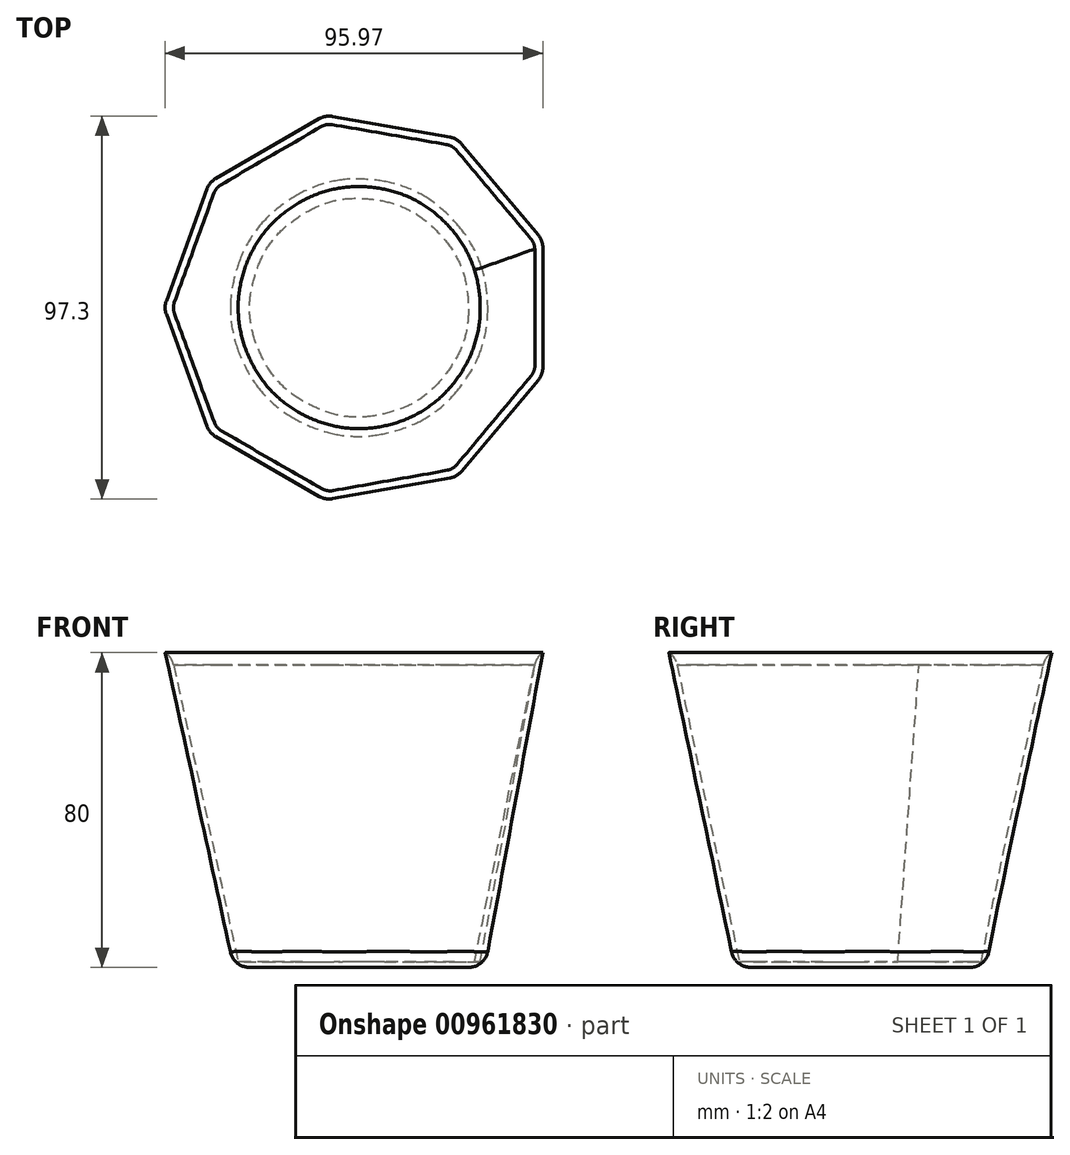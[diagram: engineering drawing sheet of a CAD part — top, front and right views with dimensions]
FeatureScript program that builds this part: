
annotation { "Feature Type Name" : "Feature", "Feature Type Description" : "" }
export const myFeature = defineFeature(function(context is Context, id is Id, definition is map)
    precondition{}
    {
        {
            var Q0;
            Q0=qCreatedBy(makeId("Top.planeOp"),FACE);
            var sketch = newSketch(context, id + "F0", { "sketchPlane" : qUnion([Q0])});
            skCircle(sketch, "E0", {"center": v(0, 0) * mm, "radius": 31.9 * mm});
            skSolve(sketch);
        }
        {
            var Q0;
            Q0=qCreatedBy(makeId("Top.planeOp"),FACE);
            cPlane(context, id + "F1", {"entities" : qUnion([Q0]), "cplaneType" : CPlaneType.OFFSET, "offset" : 80 * mm, "width" : 150 * mm, "height" : 150 * mm});
        }
        {
            var Q0;
            Q0=qCreatedBy(id+"F1.planeOp",FACE);
            var sketch = newSketch(context, id + "F2", { "sketchPlane" : qUnion([Q0])});
            skCircle(sketch, "E1.cCircle", {"center": v(0, 0) * mm, "radius": 46.65 * mm, "construction": true});
            skLineSegment(sketch, "E1.0", {"start": v(46.65, 15.16) * mm, "end": v(46.65, -15.16) * mm});
            skLineSegment(sketch, "E1.1", {"start": v(45.48, -18.37) * mm, "end": v(25.99, -41.6) * mm});
            skLineSegment(sketch, "E1.2", {"start": v(23.03, -43.3) * mm, "end": v(-6.83, -48.57) * mm});
            skLineSegment(sketch, "E1.3", {"start": v(-10.2, -47.98) * mm, "end": v(-36.45, -32.82) * mm});
            skLineSegment(sketch, "E1.4", {"start": v(-38.65, -30.2) * mm, "end": v(-49.02, -1.71) * mm});
            skLineSegment(sketch, "E1.5", {"start": v(-49.02, 1.71) * mm, "end": v(-38.65, 30.2) * mm});
            skLineSegment(sketch, "E1.6", {"start": v(-36.45, 32.82) * mm, "end": v(-10.2, 47.98) * mm});
            skLineSegment(sketch, "E1.7", {"start": v(-6.83, 48.57) * mm, "end": v(23.03, 43.3) * mm});
            skLineSegment(sketch, "E1.8", {"start": v(25.99, 41.6) * mm, "end": v(45.48, 18.37) * mm});
            skPoint(sketch, "E1.0.midPoint", {"position": v(46.65, 0) * mm});
            skPoint(sketch, "E2.visualSharp", {"position": v(-8.62, 48.89) * mm});
            skArc(sketch, "E2.filletArc", {"start": v(-6.83, 48.57) * mm, "mid": v(-8.56, 48.57) * mm, "end": v(-10.2, 47.98) * mm});
            skPoint(sketch, "E3.visualSharp", {"position": v(46.65, 16.98) * mm});
            skArc(sketch, "E3.filletArc", {"start": v(46.65, 15.16) * mm, "mid": v(46.34, 16.87) * mm, "end": v(45.48, 18.37) * mm});
            skPoint(sketch, "E4.visualSharp", {"position": v(46.65, -16.98) * mm});
            skArc(sketch, "E4.filletArc", {"start": v(45.48, -18.37) * mm, "mid": v(46.34, -16.87) * mm, "end": v(46.65, -15.16) * mm});
            skPoint(sketch, "E5.visualSharp", {"position": v(24.82, -42.99) * mm});
            skArc(sketch, "E5.filletArc", {"start": v(23.03, -43.3) * mm, "mid": v(24.66, -42.71) * mm, "end": v(25.99, -41.6) * mm});
            skPoint(sketch, "E6.visualSharp", {"position": v(-8.62, -48.89) * mm});
            skArc(sketch, "E6.filletArc", {"start": v(-10.2, -47.98) * mm, "mid": v(-8.56, -48.57) * mm, "end": v(-6.83, -48.57) * mm});
            skPoint(sketch, "E7.visualSharp", {"position": v(-38.03, -31.9) * mm});
            skArc(sketch, "E7.filletArc", {"start": v(-38.65, -30.2) * mm, "mid": v(-37.78, -31.7) * mm, "end": v(-36.45, -32.82) * mm});
            skPoint(sketch, "E8.visualSharp", {"position": v(-49.64, 0) * mm});
            skArc(sketch, "E8.filletArc", {"start": v(-49.02, 1.71) * mm, "mid": v(-49.32, 0) * mm, "end": v(-49.02, -1.71) * mm});
            skPoint(sketch, "E9.visualSharp", {"position": v(-38.03, 31.9) * mm});
            skArc(sketch, "E9.filletArc", {"start": v(-36.45, 32.82) * mm, "mid": v(-37.78, 31.7) * mm, "end": v(-38.65, 30.2) * mm});
            skPoint(sketch, "E10.visualSharp", {"position": v(24.82, 42.99) * mm});
            skArc(sketch, "E10.filletArc", {"start": v(25.99, 41.6) * mm, "mid": v(24.66, 42.71) * mm, "end": v(23.03, 43.3) * mm});
            skSolve(sketch);
        }
        {
            var Q0;
            Q0=makeQuery(id+"F0.imprint","IMPRINT",FACE,{"disambiguationData":[TD([[makeQuery(id+"F0.imprint","IMPRINT",EDGE,{"derivedFrom":sQuery(id+"F0.wireOp",EDGE,"E0")}),1.0]])]});
            var Q1;
            Q1=makeQuery(id+"F2.imprint","IMPRINT",FACE,{"disambiguationData":[TD([[makeQuery(id+"F2.imprint","IMPRINT",EDGE,{"derivedFrom":sQuery(id+"F2.wireOp",EDGE,"E1.0")}),-1.0]])]});
            loft(context, id + "F3", {"sheetProfilesArray" : [{ "sheetProfileEntities" : qUnion([Q0]) }, { "sheetProfileEntities" : qUnion([Q1]) }]});
        }
        {
            var Q0;
            Q0=makeQuery(id+"F3.opLoft","CAP_FACE",FACE,{"disambiguationData":[OSD([makeQuery(id+"F2.imprint","IMPRINT",FACE,{"disambiguationData":[TD([[makeQuery(id+"F2.imprint","IMPRINT",EDGE,{"derivedFrom":sQuery(id+"F2.wireOp",EDGE,"E1.0")}),-1.0]])]})])],"isStart":true});
            shell(context, id + "F4", {"entities" : qUnion([Q0]), "thickness" : 1.4 * mm});
        }
        {
            var Q0;
            Q0=makeQuery(id+"F4.opShell","OFFSET_EDGE",EDGE,{"disambiguationData":[OSD([sQuery(id+"F0.wireOp",EDGE,"E0"),sQuery(id+"F2.wireOp",EDGE,"E1.7"),sQuery(id+"F2.wireOp",EDGE,"E2.filletArc"),sQuery(id+"F2.wireOp",EDGE,"E10.filletArc")])]});
            fillet(context, id + "F5", {"entities" : qUnion([Q0]), "radius" : 5 * mm, "tangentPropagation" : true, "allowEdgeOverflow" : false});
        }
        {
            var Q0;
            Q0=makeQuery(id+"F3.opLoft","CAP_FACE",FACE,{"disambiguationData":[OSD([makeQuery(id+"F0.imprint","IMPRINT",FACE,{"disambiguationData":[TD([[makeQuery(id+"F0.imprint","IMPRINT",EDGE,{"derivedFrom":sQuery(id+"F0.wireOp",EDGE,"E0")}),1.0]])]})])],"isStart":true});
            fillet(context, id + "F6", {"entities" : qUnion([Q0]), "radius" : 5 * mm, "tangentPropagation" : true, "allowEdgeOverflow" : false});
        }
    });
